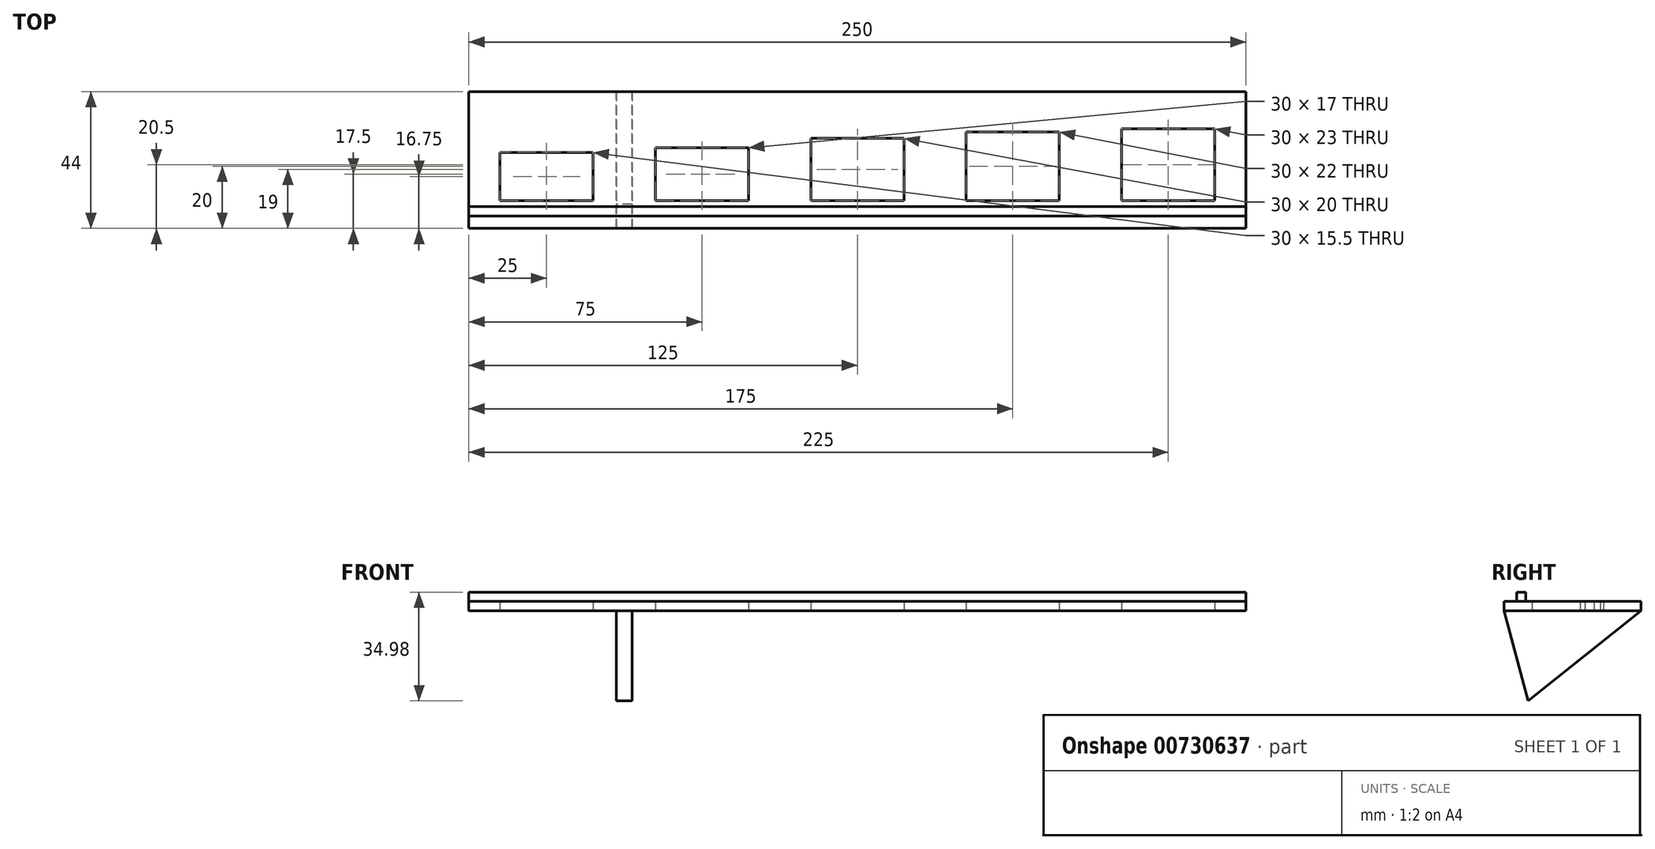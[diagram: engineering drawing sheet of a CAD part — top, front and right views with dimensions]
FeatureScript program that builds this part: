
annotation { "Feature Type Name" : "Feature", "Feature Type Description" : "" }
export const myFeature = defineFeature(function(context is Context, id is Id, definition is map)
    precondition{}
    {
        {
            var Q0;
            Q0=qCreatedBy(makeId("Top.planeOp"),FACE);
            var sketch = newSketch(context, id + "F0", { "sketchPlane" : qUnion([Q0])});
            skLineSegment(sketch, "E0.bottom", {"start": v(0, 0) * mm, "end": v(250, 0) * mm});
            skLineSegment(sketch, "E0.top", {"start": v(0, 44) * mm, "end": v(250, 44) * mm});
            skLineSegment(sketch, "E0.left", {"start": v(0, 0) * mm, "end": v(0, 44) * mm});
            skLineSegment(sketch, "E0.right", {"start": v(250, 0) * mm, "end": v(250, 44) * mm});
            skLineSegment(sketch, "E1", {"start": v(-22.5, 7) * mm, "end": v(211.98, 7) * mm, "construction": true});
            skCircle(sketch, "E2", {"center": v(25, 15.38) * mm, "radius": 8.38 * mm, "construction": true});
            skCircle(sketch, "E3", {"center": v(75, 16.25) * mm, "radius": 9.25 * mm, "construction": true});
            skCircle(sketch, "E4", {"center": v(125, 17.5) * mm, "radius": 10.5 * mm, "construction": true});
            skCircle(sketch, "E5", {"center": v(175, 18.5) * mm, "radius": 11.5 * mm, "construction": true});
            skCircle(sketch, "E6", {"center": v(225, 19.32) * mm, "radius": 12.32 * mm, "construction": true});
            skLineSegment(sketch, "E7", {"start": v(-25.6, 9) * mm, "end": v(209.93, 9) * mm, "construction": true});
            skLineSegment(sketch, "E8.bottom", {"start": v(10, 9) * mm, "end": v(40, 9) * mm});
            skLineSegment(sketch, "E8.top", {"start": v(10, 24.5) * mm, "end": v(40, 24.5) * mm});
            skLineSegment(sketch, "E8.left", {"start": v(10, 9) * mm, "end": v(10, 24.5) * mm});
            skLineSegment(sketch, "E8.right", {"start": v(40, 9) * mm, "end": v(40, 24.5) * mm});
            skLineSegment(sketch, "E9.bottom", {"start": v(110, 9) * mm, "end": v(140, 9) * mm});
            skLineSegment(sketch, "E9.top", {"start": v(110, 29) * mm, "end": v(140, 29) * mm});
            skLineSegment(sketch, "E9.left", {"start": v(110, 9) * mm, "end": v(110, 29) * mm});
            skLineSegment(sketch, "E9.right", {"start": v(140, 9) * mm, "end": v(140, 29) * mm});
            skLineSegment(sketch, "E10.bottom", {"start": v(160, 9) * mm, "end": v(190, 9) * mm});
            skLineSegment(sketch, "E10.top", {"start": v(160, 31) * mm, "end": v(190, 31) * mm});
            skLineSegment(sketch, "E10.left", {"start": v(160, 9) * mm, "end": v(160, 31) * mm});
            skLineSegment(sketch, "E10.right", {"start": v(190, 9) * mm, "end": v(190, 31) * mm});
            skLineSegment(sketch, "E11.bottom", {"start": v(210, 9) * mm, "end": v(240, 9) * mm});
            skLineSegment(sketch, "E11.top", {"start": v(210, 32) * mm, "end": v(240, 32) * mm});
            skLineSegment(sketch, "E11.left", {"start": v(210, 9) * mm, "end": v(210, 32) * mm});
            skLineSegment(sketch, "E11.right", {"start": v(240, 9) * mm, "end": v(240, 32) * mm});
            skLineSegment(sketch, "E12.bottom", {"start": v(60, 9) * mm, "end": v(90, 9) * mm});
            skLineSegment(sketch, "E12.top", {"start": v(60, 26) * mm, "end": v(90, 26) * mm});
            skLineSegment(sketch, "E12.left", {"start": v(60, 9) * mm, "end": v(60, 26) * mm});
            skLineSegment(sketch, "E12.right", {"start": v(90, 9) * mm, "end": v(90, 26) * mm});
            skSolve(sketch);
        }
        {
            var Q0;
            Q0=makeQuery(id+"F0.imprint","IMPRINT",FACE,{"disambiguationData":[TD([[makeQuery(id+"F0.imprint","IMPRINT",EDGE,{"derivedFrom":sQuery(id+"F0.wireOp",EDGE,"E0.bottom")}),1.0]])]});
            extrude(context, id + "F1", {"entities" : qUnion([Q0]), "depth" : 3 * mm, "offsetDistance" : 25 * mm});
        }
        {
            var Q0;
            Q0=makeQuery(id+"F1.opExtrude","CAP_FACE",FACE,{"disambiguationData":[OSD([sQuery(id+"F0.wireOp",EDGE,"E0.bottom"),sQuery(id+"F0.wireOp",EDGE,"E0.top"),sQuery(id+"F0.wireOp",EDGE,"E0.left"),sQuery(id+"F0.wireOp",EDGE,"E0.right"),sQuery(id+"F0.wireOp",EDGE,"E8.bottom"),sQuery(id+"F0.wireOp",EDGE,"E8.top"),sQuery(id+"F0.wireOp",EDGE,"E8.left"),sQuery(id+"F0.wireOp",EDGE,"E8.right"),sQuery(id+"F0.wireOp",EDGE,"E9.bottom"),sQuery(id+"F0.wireOp",EDGE,"E9.top"),sQuery(id+"F0.wireOp",EDGE,"E9.left"),sQuery(id+"F0.wireOp",EDGE,"E9.right"),sQuery(id+"F0.wireOp",EDGE,"E10.bottom"),sQuery(id+"F0.wireOp",EDGE,"E10.top"),sQuery(id+"F0.wireOp",EDGE,"E10.left"),sQuery(id+"F0.wireOp",EDGE,"E10.right"),sQuery(id+"F0.wireOp",EDGE,"E11.bottom"),sQuery(id+"F0.wireOp",EDGE,"E11.top"),sQuery(id+"F0.wireOp",EDGE,"E11.left"),sQuery(id+"F0.wireOp",EDGE,"E11.right"),sQuery(id+"F0.wireOp",EDGE,"E12.bottom"),sQuery(id+"F0.wireOp",EDGE,"E12.top"),sQuery(id+"F0.wireOp",EDGE,"E12.left"),sQuery(id+"F0.wireOp",EDGE,"E12.right")])],"isStart":false});
            var sketch = newSketch(context, id + "F2", { "sketchPlane" : qUnion([Q0])});
            skLineSegment(sketch, "E13.bottom", {"start": v(0, 7) * mm, "end": v(250, 7) * mm});
            skLineSegment(sketch, "E13.top", {"start": v(0, 4) * mm, "end": v(250, 4) * mm});
            skLineSegment(sketch, "E13.left", {"start": v(0, 7) * mm, "end": v(0, 4) * mm});
            skLineSegment(sketch, "E13.right", {"start": v(250, 7) * mm, "end": v(250, 4) * mm});
            skSolve(sketch);
        }
        {
            var Q0;
            Q0=makeQuery(id+"F2.imprint","IMPRINT",FACE,{"disambiguationData":[TD([[makeQuery(id+"F2.imprint","IMPRINT",EDGE,{"derivedFrom":sQuery(id+"F2.wireOp",EDGE,"E13.bottom")}),-1.0]])]});
            extrude(context, id + "F3", {"entities" : qUnion([Q0]), "depth" : 3 * mm, "offsetDistance" : 25 * mm});
        }
        {
            var Q0;
            Q0=qCreatedBy(makeId("Right.planeOp"),FACE);
            cPlane(context, id + "F4", {"entities" : qUnion([Q0]), "cplaneType" : CPlaneType.OFFSET, "offset" : 50 * mm, "width" : 150 * mm, "height" : 150 * mm});
        }
        {
            var Q0;
            Q0=qCreatedBy(id+"F4.planeOp",FACE);
            var sketch = newSketch(context, id + "F5", { "sketchPlane" : qUnion([Q0])});
            skLineSegment(sketch, "E14", {"start": v(0, 0) * mm, "end": v(44, 0) * mm});
            skLineSegment(sketch, "E15", {"start": v(44, 0) * mm, "end": v(7.76, -28.98) * mm});
            skLineSegment(sketch, "E16", {"start": v(7.76, -28.98) * mm, "end": v(0, 0) * mm});
            skSolve(sketch);
        }
        {
            var Q0;
            Q0=makeQuery(id+"F5.imprint","IMPRINT",FACE,{"disambiguationData":[TD([[makeQuery(id+"F5.imprint","IMPRINT",EDGE,{"derivedFrom":sQuery(id+"F5.wireOp",EDGE,"E14")}),-1.0]])]});
            extrude(context, id + "F6", {"entities" : qUnion([Q0]), "endBound" : BoundingType.SYMMETRIC, "depth" : 5 * mm, "offsetDistance" : 25 * mm});
        }
    });
